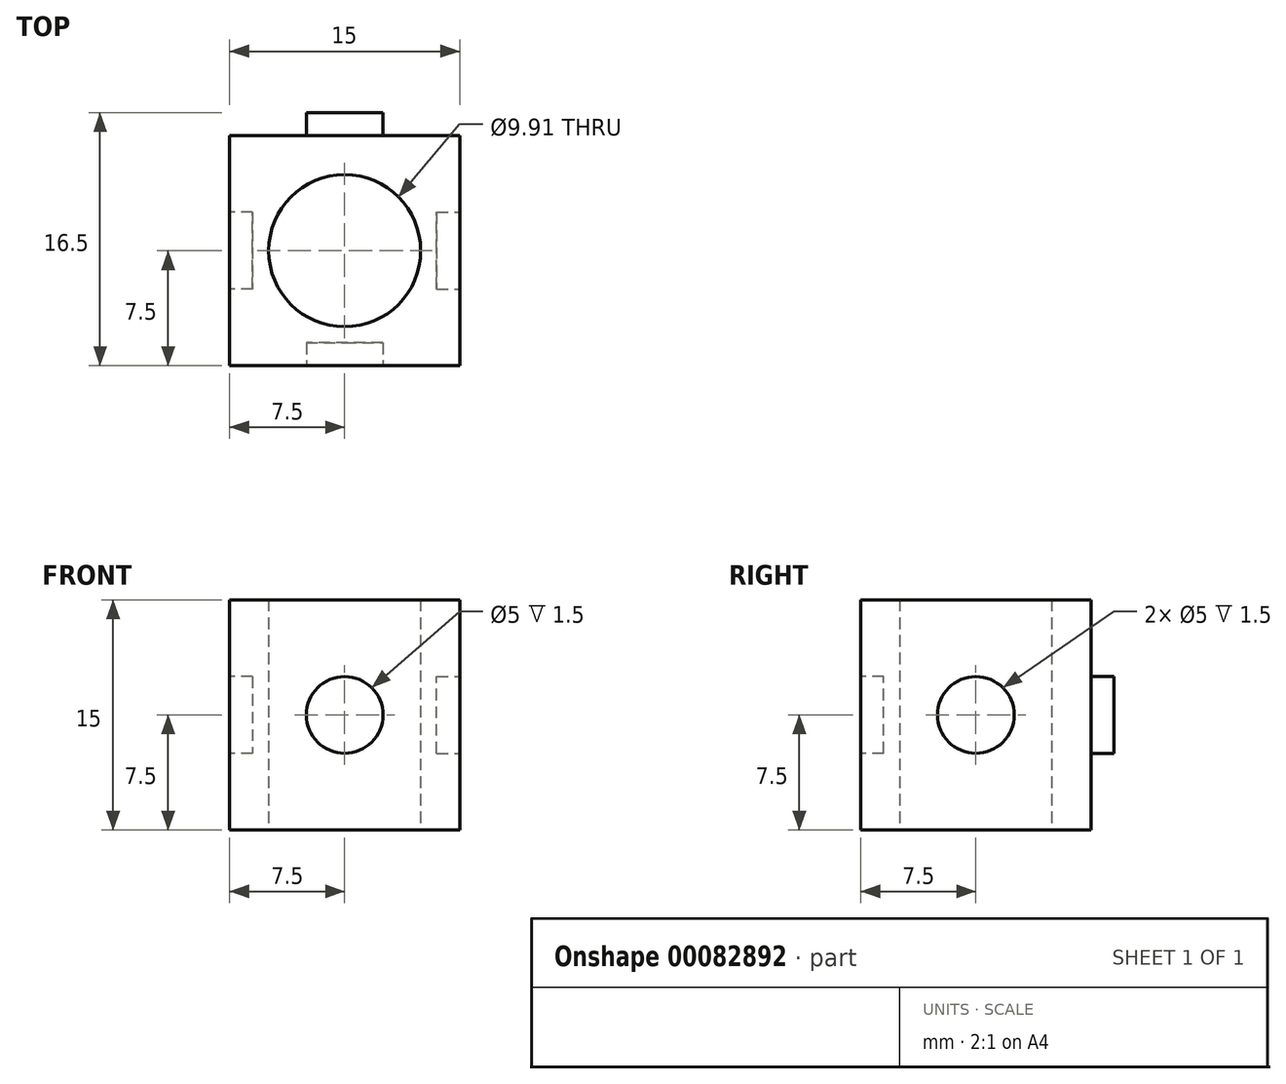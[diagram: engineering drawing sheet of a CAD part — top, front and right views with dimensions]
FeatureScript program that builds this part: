
annotation { "Feature Type Name" : "Feature", "Feature Type Description" : "" }
export const myFeature = defineFeature(function(context is Context, id is Id, definition is map)
    precondition{}
    {
        {
            var Q0;
            Q0=qCreatedBy(makeId("Top.planeOp"),FACE);
            var sketch = newSketch(context, id + "F0", { "sketchPlane" : qUnion([Q0])});
            skLineSegment(sketch, "E0.bottom", {"start": v(7.5, 7.5) * mm, "end": v(-7.5, 7.5) * mm});
            skLineSegment(sketch, "E0.top", {"start": v(7.5, -7.5) * mm, "end": v(-7.5, -7.5) * mm});
            skLineSegment(sketch, "E0.left", {"start": v(7.5, 7.5) * mm, "end": v(7.5, -7.5) * mm});
            skLineSegment(sketch, "E0.right", {"start": v(-7.5, 7.5) * mm, "end": v(-7.5, -7.5) * mm});
            skPoint(sketch, "E0.middle", {"position": v(0, 0) * mm});
            skCircle(sketch, "E1", {"center": v(0, 0) * mm, "radius": 4.96 * mm});
            skSolve(sketch);
        }
        {
            var Q0;
            Q0=makeQuery(id+"F0.imprint","IMPRINT",FACE,{"disambiguationData":[TD([[makeQuery(id+"F0.imprint","IMPRINT",EDGE,{"derivedFrom":sQuery(id+"F0.wireOp",EDGE,"E0.bottom")}),1.0]])]});
            extrude(context, id + "F1", {"entities" : qUnion([Q0]), "endBound" : BoundingType.SYMMETRIC, "depth" : 15 * mm});
        }
        {
            var Q0;
            Q0=makeQuery(id+"F1.opExtrude","SWEPT_FACE",FACE,{"disambiguationData":[OSD([sQuery(id+"F0.wireOp",EDGE,"E0.bottom")])]});
            var sketch = newSketch(context, id + "F2", { "sketchPlane" : qUnion([Q0])});
            skCircle(sketch, "E2", {"center": v(0, 0) * mm, "radius": 2.5 * mm});
            skSolve(sketch);
        }
        {
            var Q0;
            Q0=makeQuery(id+"F2.imprint","IMPRINT",FACE,{"disambiguationData":[TD([[makeQuery(id+"F2.imprint","IMPRINT",EDGE,{"derivedFrom":sQuery(id+"F2.wireOp",EDGE,"E2")}),1.0]])]});
            var Q1;
            Q1=sQuery(id+"F2.wireOp",EDGE,"E2");
            extrude(context, id + "F3", {"entities" : qUnion([Q0]), "operationType" : NewBodyOperationType.ADD, "surfaceEntities" : qUnion([Q1]), "depth" : 1.5 * mm});
        }
        {
            var Q0;
            Q0=makeQuery(id+"F1.opExtrude","SWEPT_FACE",FACE,{"disambiguationData":[OSD([sQuery(id+"F0.wireOp",EDGE,"E0.top")])]});
            var sketch = newSketch(context, id + "F4", { "sketchPlane" : qUnion([Q0])});
            skCircle(sketch, "E3", {"center": v(0, 0) * mm, "radius": 2.5 * mm});
            skSolve(sketch);
        }
        {
            var Q0;
            Q0=makeQuery(id+"F4.imprint","IMPRINT",FACE,{"disambiguationData":[TD([[makeQuery(id+"F4.imprint","IMPRINT",EDGE,{"derivedFrom":sQuery(id+"F4.wireOp",EDGE,"E3")}),1.0]])]});
            var Q1;
            Q1=sQuery(id+"F4.wireOp",EDGE,"E3");
            extrude(context, id + "F5", {"entities" : qUnion([Q0]), "operationType" : NewBodyOperationType.REMOVE, "surfaceEntities" : qUnion([Q1]), "oppositeDirection" : true, "depth" : 1.5 * mm});
        }
        {
            var Q0;
            Q0=makeQuery(id+"F1.opExtrude","SWEPT_FACE",FACE,{"disambiguationData":[OSD([sQuery(id+"F0.wireOp",EDGE,"E0.left")])]});
            var sketch = newSketch(context, id + "F6", { "sketchPlane" : qUnion([Q0])});
            skCircle(sketch, "E4", {"center": v(0, 0) * mm, "radius": 2.5 * mm});
            skSolve(sketch);
        }
        {
            var Q0;
            Q0=makeQuery(id+"F6.imprint","IMPRINT",FACE,{"disambiguationData":[TD([[makeQuery(id+"F6.imprint","IMPRINT",EDGE,{"derivedFrom":sQuery(id+"F6.wireOp",EDGE,"E4")}),1.0]])]});
            var Q1;
            Q1=sQuery(id+"F6.wireOp",EDGE,"E4");
            extrude(context, id + "F7", {"entities" : qUnion([Q0]), "operationType" : NewBodyOperationType.REMOVE, "surfaceEntities" : qUnion([Q1]), "oppositeDirection" : true, "depth" : 1.5 * mm});
        }
        {
            var Q0;
            Q0=makeQuery(id+"F1.opExtrude","SWEPT_FACE",FACE,{"disambiguationData":[OSD([sQuery(id+"F0.wireOp",EDGE,"E0.right")])]});
            var sketch = newSketch(context, id + "F8", { "sketchPlane" : qUnion([Q0])});
            skCircle(sketch, "E5", {"center": v(0, 0) * mm, "radius": 2.5 * mm});
            skSolve(sketch);
        }
        {
            var Q0;
            Q0=makeQuery(id+"F8.imprint","IMPRINT",FACE,{"disambiguationData":[TD([[makeQuery(id+"F8.imprint","IMPRINT",EDGE,{"derivedFrom":sQuery(id+"F8.wireOp",EDGE,"E5")}),1.0]])]});
            var Q1;
            Q1=sQuery(id+"F8.wireOp",EDGE,"E5");
            extrude(context, id + "F9", {"entities" : qUnion([Q0]), "operationType" : NewBodyOperationType.REMOVE, "surfaceEntities" : qUnion([Q1]), "oppositeDirection" : true, "depth" : 1.5 * mm});
        }
    });
